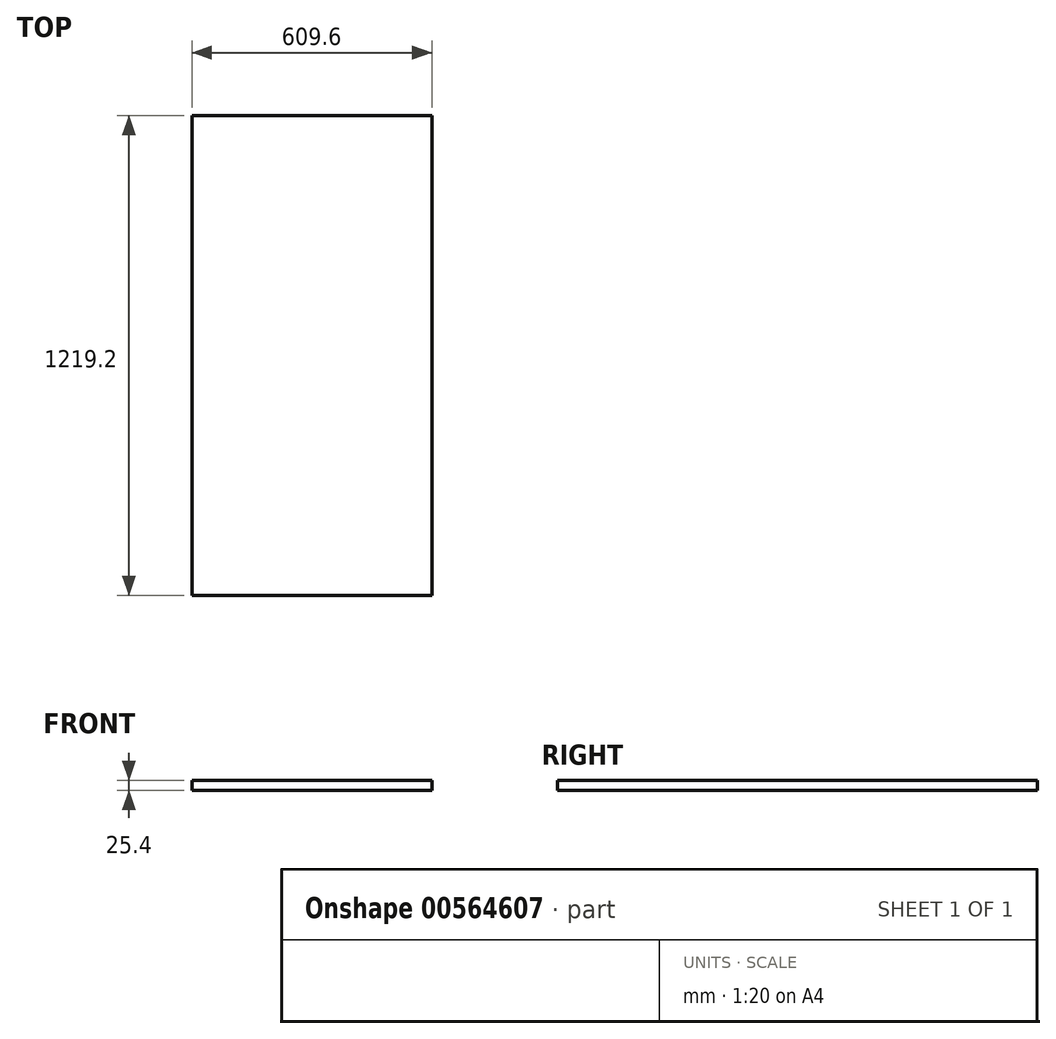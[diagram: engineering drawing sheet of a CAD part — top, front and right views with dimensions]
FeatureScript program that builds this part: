
annotation { "Feature Type Name" : "Feature", "Feature Type Description" : "" }
export const myFeature = defineFeature(function(context is Context, id is Id, definition is map)
    precondition{}
    {
        {
            var Q0;
            Q0=qCreatedBy(makeId("Top.planeOp"),FACE);
            var sketch = newSketch(context, id + "F0", { "sketchPlane" : qUnion([Q0])});
            skLineSegment(sketch, "E0.bottom", {"start": v(-28.35, 1195.4) * mm, "end": v(581.25, 1195.4) * mm});
            skLineSegment(sketch, "E0.top", {"start": v(-28.35, -23.8) * mm, "end": v(581.25, -23.8) * mm});
            skLineSegment(sketch, "E0.left", {"start": v(-28.35, 1195.4) * mm, "end": v(-28.35, -23.8) * mm});
            skLineSegment(sketch, "E0.right", {"start": v(581.25, 1195.4) * mm, "end": v(581.25, -23.8) * mm});
            skSolve(sketch);
        }
        {
            var Q0;
            Q0=makeQuery(id+"F0.imprint","IMPRINT",FACE,{"disambiguationData":[TD([[makeQuery(id+"F0.imprint","IMPRINT",EDGE,{"derivedFrom":sQuery(id+"F0.wireOp",EDGE,"E0.bottom")}),-1.0]])]});
            extrude(context, id + "F1", {"entities" : qUnion([Q0]), "depth" : 25.4 * mm, "offsetDistance" : 25.4 * mm});
        }
    });
